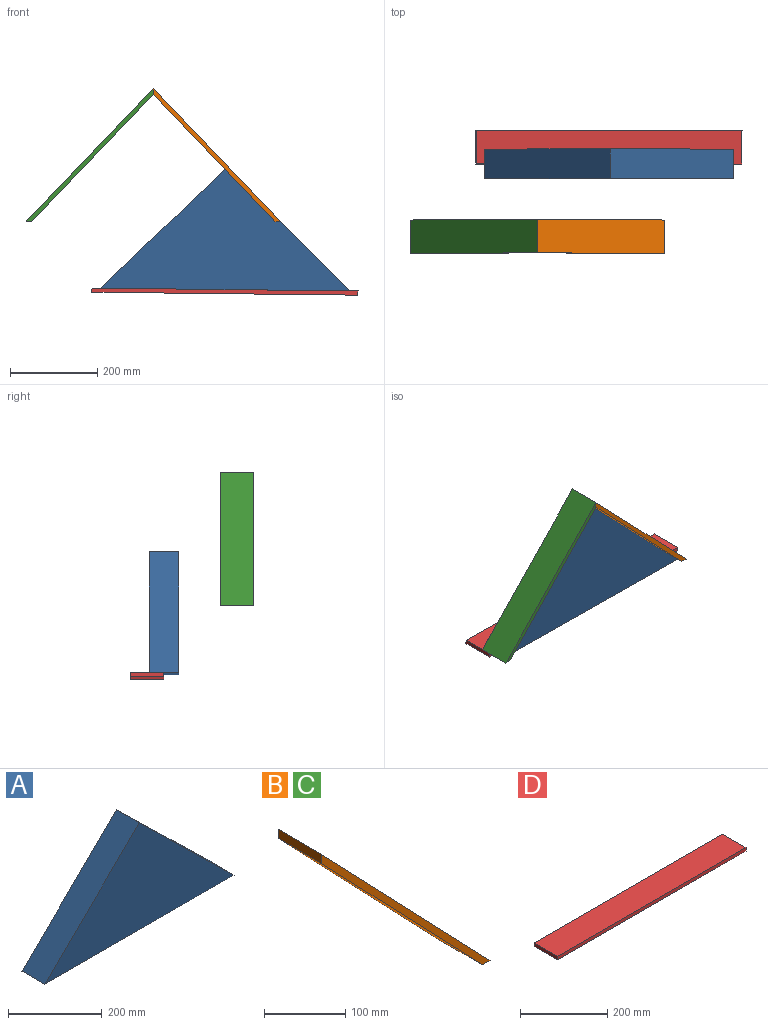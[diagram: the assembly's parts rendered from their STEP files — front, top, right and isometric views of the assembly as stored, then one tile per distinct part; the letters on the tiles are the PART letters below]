
ASSEMBLY  parts=4 mates=2
PART A: 5 faces, bbox 571.5x68.6x279.4 mm
  f0: plane 285.75x279.4mm, normal (-0.7,0,0.72), area 27407.8mm2, adj f1,f2,f3,f4
  f1: plane 571.5x68.58mm, normal (0,0,-1), area 39193.5mm2, adj f0,f2,f3,f4
  f2: plane 285.75x279.4mm, normal (0.7,0,0.72), area 27407.8mm2, adj f0,f1,f3,f4
  f3: plane 571.5x279.4mm, normal (0,-1,0), area 79838.6mm2, adj f0,f1,f2
  f4: plane 571.5x279.4mm, normal (0,1,0), area 79838.6mm2, adj f0,f1,f2
PART B: 6 faces, bbox 292.6x76.2x305.9 mm
  f0: plane 76.2x13.78mm, normal (-1,0,0), area 1050mm2, adj f1,f3,f4,f5
  f1: plane 292.1x279.4mm, normal (-0.72,0,-0.69), area 30800.9mm2, adj f0,f2,f4,f5
  f2: plane 76.2x13.18mm, normal (0,0,-1), area 1004.4mm2, adj f1,f3,f4,f5
  f3: plane 305.88x292.58mm, normal (0.72,0,0.69), area 32253.9mm2, adj f0,f2,f4,f5
  f4: plane 305.88x292.58mm, normal (0,-1,0), area 3940.9mm2, adj f0,f1,f2,f3
  f5: plane 305.88x292.58mm, normal (0,1,0), area 3940.9mm2, adj f0,f1,f2,f3
PART C: same geometry as B
PART D: 6 faces, bbox 611.2x76.2x9.5 mm
  f0: plane 611.19x76.2mm, normal (0,0,1), area 46572.5mm2, adj f1,f3,f4,f5
  f1: plane 76.2x9.53mm, normal (-1,0,0), area 725.8mm2, adj f0,f2,f4,f5
  f2: plane 611.19x76.2mm, normal (0,0,-1), area 46572.5mm2, adj f1,f3,f4,f5
  f3: plane 76.2x9.53mm, normal (1,0,0), area 725.8mm2, adj f0,f2,f4,f5
  f4: plane 611.19x9.53mm, normal (0,-1,0), area 5821.6mm2, adj f0,f1,f2,f3
  f5: plane 611.19x9.53mm, normal (0,1,0), area 5821.6mm2, adj f0,f1,f2,f3
PLACE A rot(axis=(0.01,0,1),180deg) t=(-261.11,182.76,114.79)mm
PLACE B rot(axis=(-0.72,0.68,-0.11),0deg) t=(-425.75,88.1,269.97)mm
PLACE C rot(axis=(0,0,1),180deg) t=(-425.75,11.9,269.97)mm
PLACE D rot(axis=(0,1,0),0.6deg) t=(-302.97,293.25,115.25)mm
MATE fastened D.f0 <-> A.f1  axis (0.01,0,1) through (-261.11,217.05,114.79)mm
MATE fastened B.f0 <-> C.f0  axis (-1,0,0) through (-425.75,50,568.96)mm
